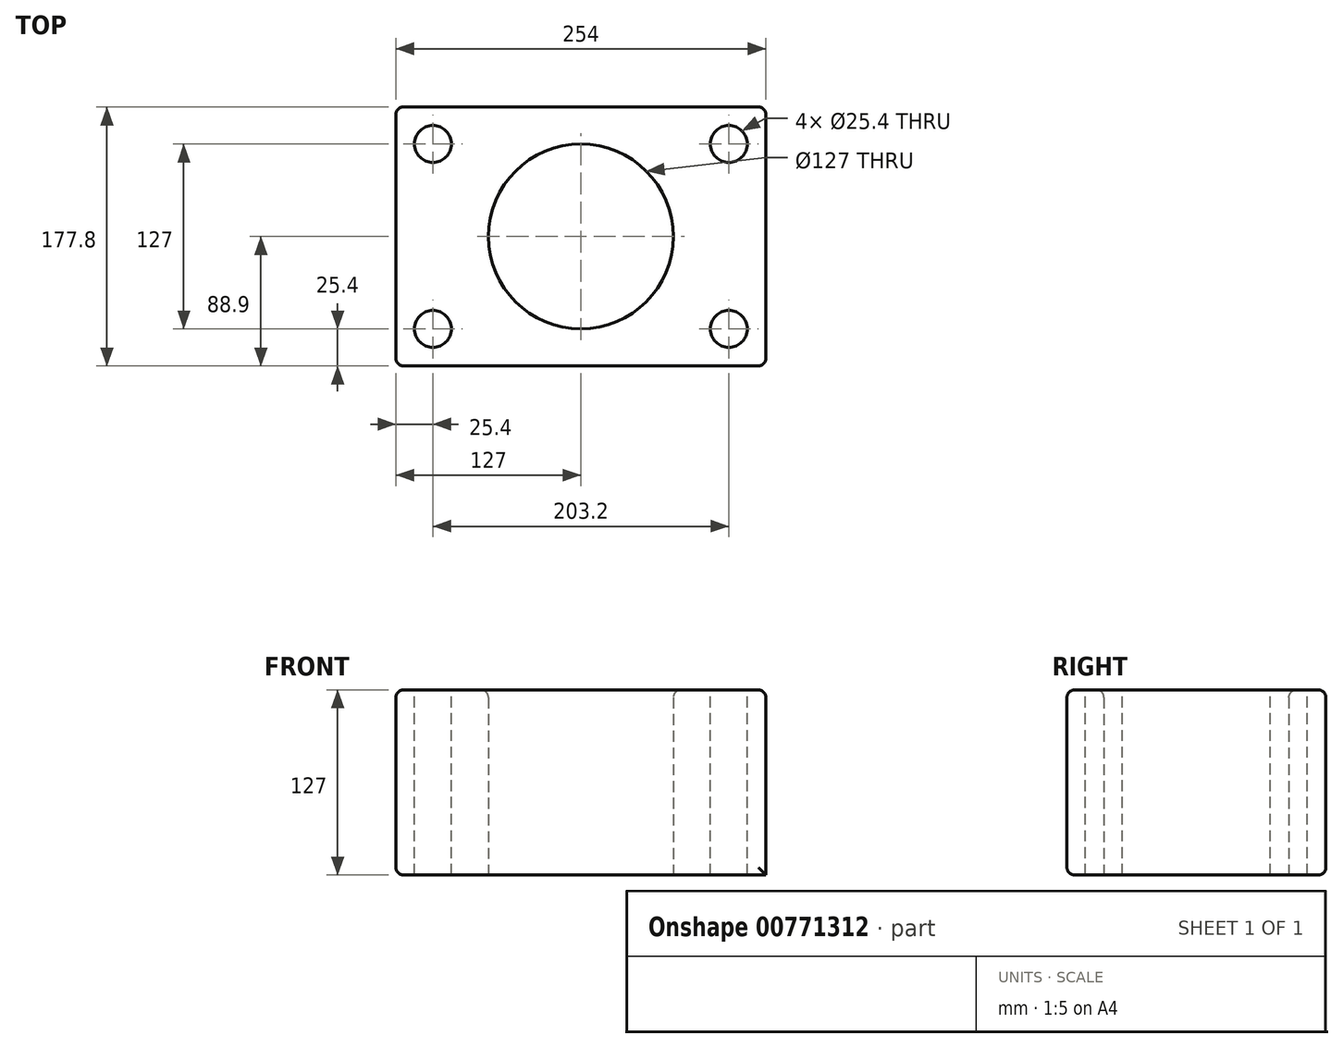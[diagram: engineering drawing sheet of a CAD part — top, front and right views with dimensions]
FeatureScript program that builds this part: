
annotation { "Feature Type Name" : "Feature", "Feature Type Description" : "" }
export const myFeature = defineFeature(function(context is Context, id is Id, definition is map)
    precondition{}
    {
        {
            var Q0;
            Q0=qCreatedBy(makeId("Top.planeOp"),FACE);
            var sketch = newSketch(context, id + "F0", { "sketchPlane" : qUnion([Q0])});
            skCircle(sketch, "E0", {"center": v(0, 0) * mm, "radius": 63.5 * mm});
            skLineSegment(sketch, "E1.bottom", {"start": v(127, -88.9) * mm, "end": v(-127, -88.9) * mm});
            skLineSegment(sketch, "E1.top", {"start": v(127, 88.9) * mm, "end": v(-127, 88.9) * mm});
            skLineSegment(sketch, "E1.left", {"start": v(127, -88.9) * mm, "end": v(127, 88.9) * mm});
            skLineSegment(sketch, "E1.right", {"start": v(-127, -88.9) * mm, "end": v(-127, 88.9) * mm});
            skSolve(sketch);
        }
        {
            var Q0;
            Q0=makeQuery(id+"F0.imprint","IMPRINT",FACE,{"disambiguationData":[TD([[makeQuery(id+"F0.imprint","IMPRINT",EDGE,{"derivedFrom":sQuery(id+"F0.wireOp",EDGE,"E0")}),-1.0]])]});
            extrude(context, id + "F1", {"entities" : qUnion([Q0]), "depth" : 127 * mm, "offsetDistance" : 25.4 * mm});
        }
        {
            var Q0;
            Q0=makeQuery(id+"F1.opExtrude","CAP_FACE",FACE,{"disambiguationData":[OSD([sQuery(id+"F0.wireOp",EDGE,"E0"),sQuery(id+"F0.wireOp",EDGE,"E1.bottom"),sQuery(id+"F0.wireOp",EDGE,"E1.top"),sQuery(id+"F0.wireOp",EDGE,"E1.left"),sQuery(id+"F0.wireOp",EDGE,"E1.right")])],"isStart":false});
            var Q1;
            Q1=makeQuery(id+"F1.opExtrude","SWEPT_FACE",FACE,{"disambiguationData":[OSD([sQuery(id+"F0.wireOp",EDGE,"E1.right")])]});
            var Q2;
            Q2=makeQuery(id+"F1.opExtrude","SWEPT_FACE",FACE,{"disambiguationData":[OSD([sQuery(id+"F0.wireOp",EDGE,"E1.bottom")])]});
            var Q3;
            Q3=makeQuery(id+"F1.opExtrude","SWEPT_FACE",FACE,{"disambiguationData":[OSD([sQuery(id+"F0.wireOp",EDGE,"E1.top")])]});
            fillet(context, id + "F2", {"entities" : qUnion([Q0, Q1, Q2, Q3]), "radius" : 5.08 * mm, "tangentPropagation" : true, "allowEdgeOverflow" : false});
        }
        {
            var Q0;
            Q0=makeQuery(id+"F1.opExtrude","CAP_FACE",FACE,{"disambiguationData":[OSD([sQuery(id+"F0.wireOp",EDGE,"E0"),sQuery(id+"F0.wireOp",EDGE,"E1.bottom"),sQuery(id+"F0.wireOp",EDGE,"E1.top"),sQuery(id+"F0.wireOp",EDGE,"E1.left"),sQuery(id+"F0.wireOp",EDGE,"E1.right")])],"isStart":false});
            var sketch = newSketch(context, id + "F3", { "sketchPlane" : qUnion([Q0])});
            skCircle(sketch, "E2", {"center": v(-101.6, 63.5) * mm, "radius": 12.7 * mm});
            skCircle(sketch, "E3.MirrorC", {"center": v(101.6, 63.5) * mm, "radius": 12.7 * mm});
            skCircle(sketch, "E4.MirrorC", {"center": v(101.6, -63.5) * mm, "radius": 12.7 * mm});
            skCircle(sketch, "E5.MirrorC", {"center": v(-101.6, -63.5) * mm, "radius": 12.7 * mm});
            skSolve(sketch);
        }
        {
            var Q0;
            Q0 = qSketchRegion(id + "F3", true);
            extrude(context, id + "F4", {"entities" : qUnion([Q0]), "operationType" : NewBodyOperationType.REMOVE, "endBound" : BoundingType.UP_TO_NEXT, "oppositeDirection" : true, "depth" : 25.4 * mm, "offsetDistance" : 25.4 * mm});
        }
    });
